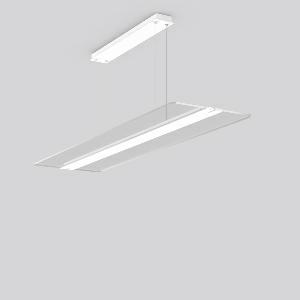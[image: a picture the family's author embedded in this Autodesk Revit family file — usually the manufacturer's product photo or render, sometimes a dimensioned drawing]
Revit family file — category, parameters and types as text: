
# Revit family: twindot_s_312263_002_dd94
name_source: partatom
category: Lighting Fixtures
units: mm (PartAtom-declared; Revit-internal decimal feet)

## family parameters
Cut with Voids When Loaded = No
Host = Face
Light Source = No
Part Type = Normal
Room Calculation Point = No
Round Connector Dimension = Use Diameter
Shared = No

## types (1)
- TWINDOT S (1 x LED Modul 830, 6500 lm, 3000)
    Apparent Load = 57 VA
    CIE Flux Codes = 47 77 94 55 100
    Color Rendering = 80
    Color Temperature = 3000
    Default Elevation = 1800 mm
    Description = Series: TWINDOT S
LED pendant luminaire with extremely flat and frameless appearance. Middle bar made of aluminium extrusion profile, powder-coated. Transparent light guide made of UV-resistant acrylic glass (PMMA) with TWINDOT prismatic. Light control with perfectly glare-free TWINDOT technology for pleasantly gentle light with soft shadows. Even and wide indirect and direct light distribution. Direct 55%, indirect 45% light emission. 4-point steel cable suspension, steplessly adjustable. Converter integrated in the canopy (powder-coated white). Power supply through suspension cable. 
Colour: traffic white, matt (RAL 9016)
Length: 1200 mm
Width: 350 mm
Height: 20 mm
Suspension length: 500-1200 mm
Lamp: LED
Socket: without socket
Colour temperature: 3000K
Colour rendering index (CRI): 80
System power: 57 W
Rated luminous flux: 6500 lm
Luminous efficiency: 114 lm/W
Control gear: Regulated power supply
Protection class: I
Type of protection: IP 20
    Height = 20 mm  [stored 0.0656168 ft]
    Lamp = 1 x LED Modul 830
    Lamp Light Flux = 6500 lm
    Lamp count = 1
    Length = 1200 mm
    Lifetime = 50000 h
    Luminous efficacy = 114 lm/W
    Manufacturer = RZB
    ModVariant = No
    Model = 312263.002
    Mounting Place = Ceiling
    Mounting Type = Pendant
    Number of Poles = 1
    OnlyDefault = Yes
    Power Factor = 1
    Product Name = TWINDOT S
    Product group = Pendant modular luminaires
    ProductGroupID = 906
    Protection Class = Protection class I
    Protection Degree = IP 20
    RLX_Detail_Level = 1
    RLX_Emergency_Light_Flux = 0 lm
    RLX_Emergency_Type = 0
    RLX_Emergency_Type_DB = No
    RlxData = <blob elided: 35305 chars, md5=add6a096>
    Socket = socket
    Standby Power = 0 W
    System Light Flux = 6500 lm
    System Power = 57 W
    Type Comments = Product without accessories
    Type Image = 312263.002.jpg
    URL = http://relux.com
    VarID = ---
    Voltage = 230 V
    Voltage Range = 220-240 V
    Weight = 0.00 kg
    Width = 350 mm

note: [stored X ft] marks values corroborated as IEEE doubles in the binary element streams (Revit-internal decimal feet)

## geometry (parser evidence)
native form markers: Blend x4, Sweep x10
no freeform markers — native parametric forms only
